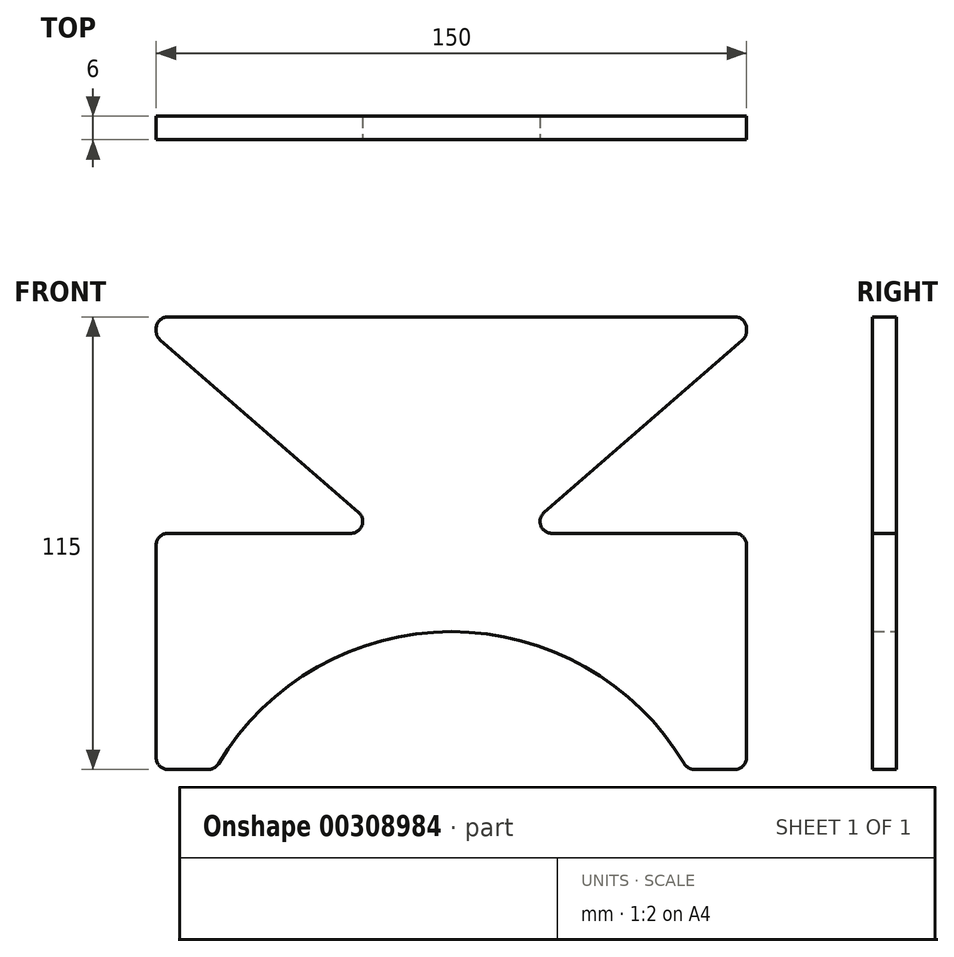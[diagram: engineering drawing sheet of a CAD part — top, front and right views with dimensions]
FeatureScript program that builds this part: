
annotation { "Feature Type Name" : "Feature", "Feature Type Description" : "" }
export const myFeature = defineFeature(function(context is Context, id is Id, definition is map)
    precondition{}
    {
        {
            var Q0;
            Q0=qCreatedBy(makeId("Front.planeOp"),FACE);
            var sketch = newSketch(context, id + "F0", { "sketchPlane" : qUnion([Q0])});
            skLineSegment(sketch, "E0.bottom", {"start": v(-75, 0) * mm, "end": v(-60, 0) * mm});
            skLineSegment(sketch, "E0.top", {"start": v(-75, 115) * mm, "end": v(75, 115) * mm});
            skLineSegment(sketch, "E0.left", {"start": v(-75, 0) * mm, "end": v(-75, 60) * mm});
            skLineSegment(sketch, "E0.right", {"start": v(75, 0) * mm, "end": v(75, 60) * mm});
            skLineSegment(sketch, "E1", {"start": v(-75, 0) * mm, "end": v(0, -75) * mm, "construction": true});
            skLineSegment(sketch, "E2", {"start": v(0, -75) * mm, "end": v(75, 0) * mm, "construction": true});
            skLineSegment(sketch, "E3", {"start": v(-75, 0) * mm, "end": v(0, 75) * mm, "construction": true});
            skLineSegment(sketch, "E4", {"start": v(0, 75) * mm, "end": v(75, 0) * mm, "construction": true});
            skLineSegment(sketch, "E5", {"start": v(-75, 60) * mm, "end": v(-17.5, 60) * mm});
            skLineSegment(sketch, "E6", {"start": v(-17.5, 60) * mm, "end": v(-75, 110) * mm});
            skLineSegment(sketch, "E7.trimOffspring", {"start": v(-75, 110) * mm, "end": v(-75, 115) * mm});
            skLineSegment(sketch, "E8", {"start": v(75, 60) * mm, "end": v(17.5, 60) * mm});
            skLineSegment(sketch, "E9", {"start": v(17.5, 60) * mm, "end": v(75, 110) * mm});
            skLineSegment(sketch, "E10.trimOffspring", {"start": v(75, 110) * mm, "end": v(75, 115) * mm});
            skLineSegment(sketch, "E11", {"start": v(-17.5, 60) * mm, "end": v(17.5, 60) * mm, "construction": true});
            skPoint(sketch, "E12", {"position": v(0, 60) * mm});
            skArc(sketch, "E13", {"start": v(60, 0) * mm, "mid": v(0, 35) * mm, "end": v(-60, 0) * mm});
            skLineSegment(sketch, "E14.trimOffspring", {"start": v(60, 0) * mm, "end": v(75, 0) * mm});
            skSolve(sketch);
        }
        {
            var Q0;
            Q0=makeQuery(id+"F0.imprint","IMPRINT",FACE,{"disambiguationData":[TD([[makeQuery(id+"F0.imprint","IMPRINT",EDGE,{"derivedFrom":sQuery(id+"F0.wireOp",EDGE,"E0.bottom")}),1.0]])]});
            extrude(context, id + "F1", {"entities" : qUnion([Q0]), "endBound" : BoundingType.SYMMETRIC, "depth" : 6 * mm});
        }
        {
            var Q0;
            Q0=makeQuery(id+"F1.opExtrude","SWEPT_EDGE",EDGE,{"disambiguationData":[OSD([sQuery(id+"F0.wireOp",EDGE,"E5"),sQuery(id+"F0.wireOp",EDGE,"E6")])]});
            var Q1;
            Q1=makeQuery(id+"F1.opExtrude","SWEPT_EDGE",EDGE,{"disambiguationData":[OSD([sQuery(id+"F0.wireOp",EDGE,"E8"),sQuery(id+"F0.wireOp",EDGE,"E9")])]});
            var Q2;
            Q2=makeQuery(id+"F1.opExtrude","SWEPT_EDGE",EDGE,{"disambiguationData":[OSD([sQuery(id+"F0.wireOp",EDGE,"E0.right"),sQuery(id+"F0.wireOp",EDGE,"E8")])]});
            var Q3;
            Q3=makeQuery(id+"F1.opExtrude","SWEPT_EDGE",EDGE,{"disambiguationData":[OSD([sQuery(id+"F0.wireOp",EDGE,"E0.right"),sQuery(id+"F0.wireOp",EDGE,"E14.trimOffspring")])]});
            var Q4;
            Q4=makeQuery(id+"F1.opExtrude","SWEPT_EDGE",EDGE,{"disambiguationData":[OSD([sQuery(id+"F0.wireOp",EDGE,"E0.bottom"),sQuery(id+"F0.wireOp",EDGE,"E13")])]});
            var Q5;
            Q5=makeQuery(id+"F1.opExtrude","SWEPT_EDGE",EDGE,{"disambiguationData":[OSD([sQuery(id+"F0.wireOp",EDGE,"E0.left"),sQuery(id+"F0.wireOp",EDGE,"E5")])]});
            var Q6;
            Q6=makeQuery(id+"F1.opExtrude","SWEPT_EDGE",EDGE,{"disambiguationData":[OSD([sQuery(id+"F0.wireOp",EDGE,"E13"),sQuery(id+"F0.wireOp",EDGE,"E14.trimOffspring")])]});
            var Q7;
            Q7=makeQuery(id+"F1.opExtrude","SWEPT_EDGE",EDGE,{"disambiguationData":[OSD([sQuery(id+"F0.wireOp",EDGE,"E0.bottom"),sQuery(id+"F0.wireOp",EDGE,"E0.left")])]});
            var Q8;
            Q8=makeQuery(id+"F1.opExtrude","SWEPT_EDGE",EDGE,{"disambiguationData":[OSD([sQuery(id+"F0.wireOp",EDGE,"E0.top"),sQuery(id+"F0.wireOp",EDGE,"E7.trimOffspring")])]});
            var Q9;
            Q9=makeQuery(id+"F1.opExtrude","SWEPT_EDGE",EDGE,{"disambiguationData":[OSD([sQuery(id+"F0.wireOp",EDGE,"E6"),sQuery(id+"F0.wireOp",EDGE,"E7.trimOffspring")])]});
            var Q10;
            Q10=makeQuery(id+"F1.opExtrude","SWEPT_EDGE",EDGE,{"disambiguationData":[OSD([sQuery(id+"F0.wireOp",EDGE,"E0.top"),sQuery(id+"F0.wireOp",EDGE,"E10.trimOffspring")])]});
            var Q11;
            Q11=makeQuery(id+"F1.opExtrude","SWEPT_EDGE",EDGE,{"disambiguationData":[OSD([sQuery(id+"F0.wireOp",EDGE,"E9"),sQuery(id+"F0.wireOp",EDGE,"E10.trimOffspring")])]});
            fillet(context, id + "F2", {"entities" : qUnion([Q0, Q1, Q2, Q3, Q4, Q5, Q6, Q7, Q8, Q9, Q10, Q11]), "radius" : 3 * mm, "tangentPropagation" : true, "allowEdgeOverflow" : false});
        }
    });
